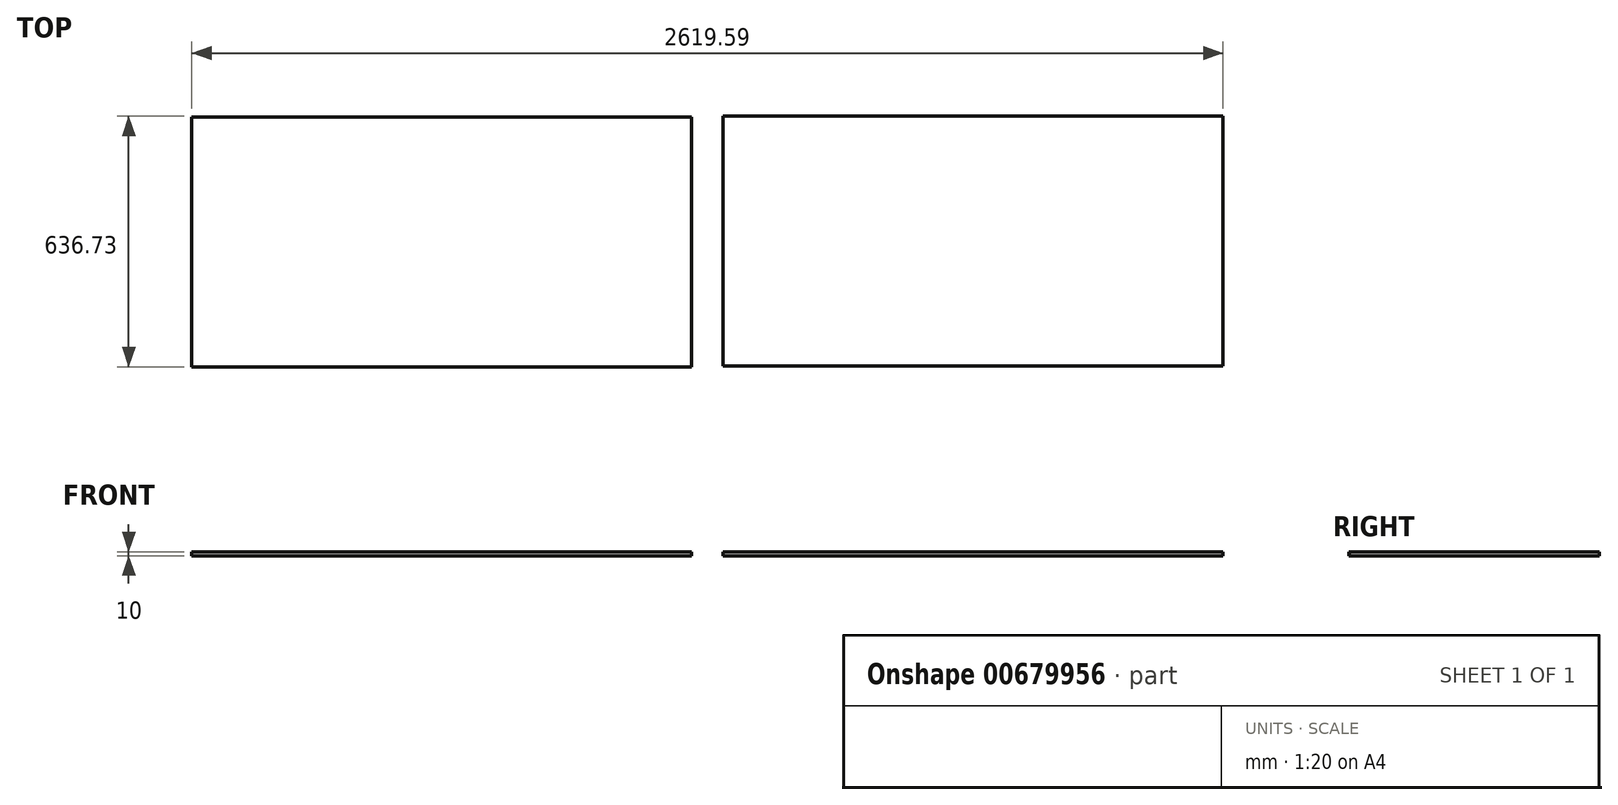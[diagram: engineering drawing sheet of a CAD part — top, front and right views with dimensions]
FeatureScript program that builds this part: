
annotation { "Feature Type Name" : "Feature", "Feature Type Description" : "" }
export const myFeature = defineFeature(function(context is Context, id is Id, definition is map)
    precondition{}
    {
        {
            assignVariable(context, id + "F0", {"name" : "thickness", "anyValue" : 10});
        }
        {
            var Q0;
            Q0=qCreatedBy(makeId("Top.planeOp"),FACE);
            var sketch = newSketch(context, id + "F1", { "sketchPlane" : qUnion([Q0])});
            skLineSegment(sketch, "E0.bottom", {"start": v(-1270, 635) * mm, "end": v(0, 635) * mm});
            skLineSegment(sketch, "E0.top", {"start": v(-1270, 0) * mm, "end": v(0, 0) * mm});
            skLineSegment(sketch, "E0.left", {"start": v(-1270, 635) * mm, "end": v(-1270, 0) * mm});
            skLineSegment(sketch, "E0.right", {"start": v(0, 635) * mm, "end": v(0, 0) * mm});
            skLineSegment(sketch, "E1.bottom", {"start": v(79.6, 636.73) * mm, "end": v(1349.6, 636.73) * mm});
            skLineSegment(sketch, "E1.top", {"start": v(79.6, 1.73) * mm, "end": v(1349.6, 1.73) * mm});
            skLineSegment(sketch, "E1.left", {"start": v(79.6, 636.73) * mm, "end": v(79.6, 1.73) * mm});
            skLineSegment(sketch, "E1.right", {"start": v(1349.6, 636.73) * mm, "end": v(1349.6, 1.73) * mm});
            skSolve(sketch);
        }
        {
            var Q0;
            Q0=makeQuery(id+"F1.imprint","IMPRINT",FACE,{"disambiguationData":[TD([[makeQuery(id+"F1.imprint","IMPRINT",EDGE,{"derivedFrom":sQuery(id+"F1.wireOp",EDGE,"E0.bottom")}),-1.0]])]});
            var Q1;
            Q1=makeQuery(id+"F1.imprint","IMPRINT",FACE,{"disambiguationData":[TD([[makeQuery(id+"F1.imprint","IMPRINT",EDGE,{"derivedFrom":sQuery(id+"F1.wireOp",EDGE,"E1.bottom")}),-1.0]])]});
            extrude(context, id + "F2", {"entities" : qUnion([Q0, Q1]), "depth" : (getVariable(context, 'thickness')) * mm, "offsetDistance" : 25.4 * mm});
        }
    });
